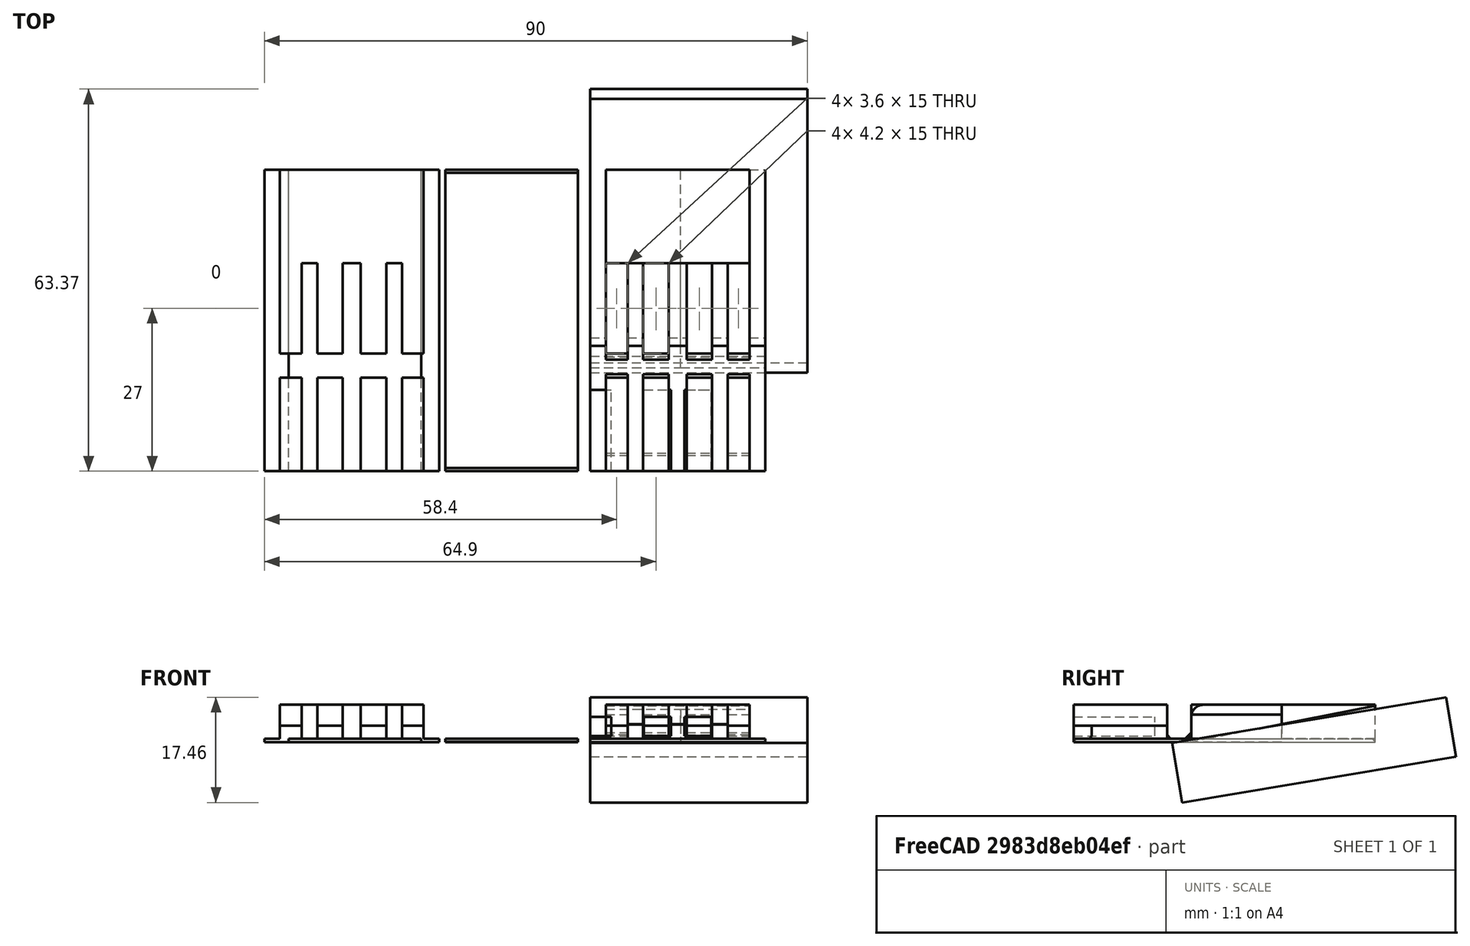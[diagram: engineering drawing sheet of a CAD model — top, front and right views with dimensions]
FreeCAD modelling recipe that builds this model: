
FCSTD DOCUMENT  (FreeCAD 0.19R24267 +99 (Git))
Label: TEST
License: All rights reserved
LicenseURL: http://en.wikipedia.org/wiki/All_rights_reserved
objects: Part::Box×15, Part::Cut×7, Part::Feature×5, Part::Chamfer×5, Mesh::Feature×4, PartDesign::FeatureBase×1, Sketcher::SketchObject×1, PartDesign::Pad×1, PartDesign::Body×1, Part::MultiFuse×1, Part::Fillet×1
note: 39 computed .brp shape members not serialized (recipe doc carries the construction recipe); baked Part::Feature solids carry a one-line shape summary decoded from their .brp

FEATURE [Part::Box] Box  label="Cube"
  AttacherType = Attacher::AttachEngine3D
  Height = 0.6
  Length = 29
  Width = 50
FEATURE [Part::Box] Box001  label="Cube001"
  AttacherType = Attacher::AttachEngine3D
  Height = 0.6
  Length = 22
  Placement = pos=(-50,0,0) rot=(0,0,1;0rad)
  Width = 50
FEATURE [Part::Box] Box002  label="Cube002"
  AttacherType = Attacher::AttachEngine3D
  Height = 3.2
  Length = 3.5
  Placement = pos=(0,0,1) rot=(0,0,1;0rad)
  Width = 13.5
FEATURE [Part::Box] Box003  label="Cube003"
  AttacherType = Attacher::AttachEngine3D
  Height = 3.2
  Length = 4.5
  Placement = pos=(8.9,0,1) rot=(0,0,1;0rad)
  Width = 13.5
FEATURE [Part::Box] Box004  label="Cube004"
  AttacherType = Attacher::AttachEngine3D
  Height = 3.2
  Length = 4.5
  Placement = pos=(15.6,0,1) rot=(0,0,1;0rad)
  Width = 13.5
FEATURE [PartDesign::FeatureBase] BaseFeature
  BaseFeature = -> Box
FEATURE [Sketcher::SketchObject] Sketch
  FullyConstrained = true
  MapMode = 5
  Support = -> [XY_Plane]
  sketch-geometry (37):
    g0: LineSegment StartX=14.5 StartY=55 StartZ=0 EndX=14.5 EndY=-13 EndZ=0
    g1: LineSegment StartX=-8 StartY=15.5 StartZ=0 EndX=37 EndY=15.5 EndZ=0
    g2: LineSegment StartX=-8 StartY=32 StartZ=0 EndX=37 EndY=32 EndZ=0
    g3: LineSegment StartX=13.3 StartY=18.5 StartZ=0 EndX=13.3 EndY=-2.5 EndZ=0
    g4: LineSegment StartX=15.7 StartY=18.5 StartZ=0 EndX=15.7 EndY=-2.5 EndZ=0
    g5: LineSegment StartX=8.8 StartY=15.5 StartZ=0 EndX=13 EndY=15.5 EndZ=0
    g6: LineSegment StartX=13 StartY=15.5 StartZ=0 EndX=13 EndY=0 EndZ=0
    g7: LineSegment StartX=13 StartY=0 StartZ=0 EndX=8.8 EndY=0 EndZ=0
    g8: LineSegment StartX=8.8 StartY=0 StartZ=0 EndX=8.8 EndY=15.5 EndZ=0
    g9: LineSegment StartX=2.6 StartY=15.5 StartZ=0 EndX=6.2 EndY=15.5 EndZ=0
    g10: LineSegment StartX=6.2 StartY=15.5 StartZ=0 EndX=6.2 EndY=0 EndZ=0
    g11: LineSegment StartX=6.2 StartY=4e-16 StartZ=0 EndX=2.6 EndY=4e-16 EndZ=0
    g12: LineSegment StartX=2.6 StartY=4e-16 StartZ=0 EndX=2.6 EndY=15.5 EndZ=0
    g13: LineSegment StartX=16 StartY=15.5 StartZ=0 EndX=20.2 EndY=15.5 EndZ=0
    g14: LineSegment StartX=20.2 StartY=15.5 StartZ=0 EndX=20.2 EndY=0 EndZ=0
    g15: LineSegment StartX=20.2 StartY=0 StartZ=0 EndX=16 EndY=0 EndZ=0
    g16: LineSegment StartX=16 StartY=0 StartZ=0 EndX=16 EndY=15.5 EndZ=0
    g17: LineSegment StartX=22.8 StartY=15.5 StartZ=0 EndX=26.4 EndY=15.5 EndZ=0
    g18: LineSegment StartX=26.4 StartY=15.5 StartZ=0 EndX=26.4 EndY=0 EndZ=0
    g19: LineSegment StartX=26.4 StartY=0 StartZ=0 EndX=22.8 EndY=0 EndZ=0
    g20: LineSegment StartX=22.8 StartY=0 StartZ=0 EndX=22.8 EndY=15.5 EndZ=0
    g21: LineSegment StartX=2.6 StartY=34.5 StartZ=0 EndX=6.2 EndY=34.5 EndZ=0
    g22: LineSegment StartX=6.2 StartY=34.5 StartZ=0 EndX=6.2 EndY=19.5 EndZ=0
    g23: LineSegment StartX=6.2 StartY=19.5 StartZ=0 EndX=2.6 EndY=19.5 EndZ=0
    g24: LineSegment StartX=2.6 StartY=19.5 StartZ=0 EndX=2.6 EndY=34.5 EndZ=0
    g25: LineSegment StartX=8.8 StartY=34.5 StartZ=0 EndX=13 EndY=34.5 EndZ=0
    g26: LineSegment StartX=13 StartY=34.5 StartZ=0 EndX=13 EndY=19.5 EndZ=0
    g27: LineSegment StartX=13 StartY=19.5 StartZ=0 EndX=8.8 EndY=19.5 EndZ=0
    g28: LineSegment StartX=8.8 StartY=19.5 StartZ=0 EndX=8.8 EndY=34.5 EndZ=0
    g29: LineSegment StartX=16 StartY=34.5 StartZ=0 EndX=20.2 EndY=34.5 EndZ=0
    g30: LineSegment StartX=20.2 StartY=34.5 StartZ=0 EndX=20.2 EndY=19.5 EndZ=0
    g31: LineSegment StartX=20.2 StartY=19.5 StartZ=0 EndX=16 EndY=19.5 EndZ=0
    g32: LineSegment StartX=16 StartY=19.5 StartZ=0 EndX=16 EndY=34.5 EndZ=0
    g33: LineSegment StartX=22.8 StartY=34.5 StartZ=0 EndX=26.4 EndY=34.5 EndZ=0
    g34: LineSegment StartX=26.4 StartY=34.5 StartZ=0 EndX=26.4 EndY=19.5 EndZ=0
    g35: LineSegment StartX=26.4 StartY=19.5 StartZ=0 EndX=22.8 EndY=19.5 EndZ=0
    g36: LineSegment StartX=22.8 StartY=19.5 StartZ=0 EndX=22.8 EndY=34.5 EndZ=0
  constraints (112):
    c: Vertical(g0)
    c: Horizontal(g2)
    c: DistanceX(g-1,g0) = 14.5
    c: Vertical(g3)
    c: Vertical(g4)
    c: DistanceY(g-1,g1) = 15.5
    c: DistanceY(g0,g0) = 68
    c: Symmetric(g3,g4,g0)
    c: DistanceX(g3,g0) = 1.2
    c: Equal(g4,g3)
    c: DistanceY(g4,g4) = 21
    c: Symmetric(g1,g1,g0)
    c: DistanceX(g1,g1) = 45
    c: Equal(g2,g1)
    c: Vertical(g2,g1)
    c: DistanceY(g-1,g0) = 55
    c: DistanceY(g4,g-1) = 2.5
    c: DistanceY(g-1,g2) = 32
    c: Coincident(g5,g6)
    c: Coincident(g6,g7)
    c: Coincident(g7,g8)
    c: Coincident(g8,g5)
    c: Horizontal(g5)
    c: Horizontal(g7)
    c: Vertical(g6)
    c: Vertical(g8)
    c: DistanceX(g5,g5) = 4.2
    c: DistanceY(g8,g8) = 15.5
    c: DistanceX(g6,g3) = 0.3
    c: DistanceY(g5,g1) = 0
    c: Coincident(g9,g10)
    c: Coincident(g10,g11)
    c: Coincident(g11,g12)
    c: Coincident(g12,g9)
    c: Horizontal(g9)
    c: Horizontal(g11)
    c: Vertical(g10)
    c: Vertical(g12)
    c: DistanceX(g9,g9) = 3.6
    c: DistanceY(g12,g12) = 15.5
    c: DistanceY(g6,g10) = 0
    c: DistanceX(g9,g5) = 2.6
    c: Coincident(g13,g14)
    c: Coincident(g14,g15)
    c: Coincident(g15,g16)
    c: Coincident(g16,g13)
    c: Horizontal(g13)
    c: Horizontal(g15)
    c: Vertical(g14)
    c: Vertical(g16)
    c: Coincident(g17,g18)
    c: Coincident(g18,g19)
    c: Coincident(g19,g20)
    c: Coincident(g20,g17)
    c: Horizontal(g17)
    c: Horizontal(g19)
    c: Vertical(g18)
    c: Vertical(g20)
    c: Equal(g5,g13)
    c: Equal(g6,g14)
    c: Symmetric(g13,g5,g0)
    c: Equal(g20,g10)
    c: Equal(g17,g11)
    c: Symmetric(g17,g9,g0)
    c: Coincident(g21,g22)
    c: Coincident(g22,g23)
    c: Coincident(g23,g24)
    c: Coincident(g24,g21)
    c: Horizontal(g21)
    c: Horizontal(g23)
    c: Vertical(g22)
    c: Vertical(g24)
    c: Coincident(g25,g26)
    c: Coincident(g26,g27)
    c: Coincident(g27,g28)
    c: Coincident(g28,g25)
    c: Horizontal(g25)
    c: Horizontal(g27)
    c: Vertical(g26)
    c: Vertical(g28)
    c: Coincident(g29,g30)
    c: Coincident(g30,g31)
    c: Coincident(g31,g32)
    c: Coincident(g32,g29)
    c: Horizontal(g29)
    c: Horizontal(g31)
    c: Vertical(g30)
    c: Vertical(g32)
    c: Coincident(g33,g34)
    c: Coincident(g34,g35)
    c: Coincident(g35,g36)
    c: Coincident(g36,g33)
    c: Horizontal(g33)
    c: Horizontal(g35)
    c: Vertical(g34)
    c: Vertical(g36)
    c: Equal(g27,g5)
    c: Equal(g5,g31)
    c: Equal(g35,g17)
    c: Equal(g17,g23)
    c: Horizontal(g35,g30)
    c: Horizontal(g30,g26)
    c: Horizontal(g26,g22)
    c: Equal(g24,g28)
    c: Equal(g28,g32)
    c: Equal(g32,g36)
    c: Vertical(g34,g17)
    c: Vertical(g30,g13)
    c: Vertical(g27,g5)
    c: Vertical(g23,g9)
    c: DistanceY(g17,g34) = 4
    c: DistanceY(g17,g33) = 19
FEATURE [PartDesign::Pad] Pad
  BaseFeature = -> BaseFeature
  Direction = (1,1,1)
  Length = 6.2
  Length2 = 100
  Profile = -> Sketch
  Type = 0
FEATURE [PartDesign::Body] Body
  BaseFeature = -> Box
  Group = -> [BaseFeature,Sketch,Pad]
  Origin = -> Origin
  Tip = -> Pad
FEATURE [Part::Feature] Body001
  shape: bbox 29 x 50 x 4.6 mm, 62 faces (baked)
FEATURE [Part::Box] Box005  label="Cube005"
  AttacherType = Attacher::AttachEngine3D
  Height = 10
  Length = 35
  Placement = pos=(0,0,2.75) rot=(0,0,1;0rad)
  Width = 18
FEATURE [Part::Cut] Cut
  Base = -> Body001
  Tool = -> Box005
FEATURE [Part::Box] Box006  label="Cube006"
  AttacherType = Attacher::AttachEngine3D
  Height = 6.2
  Length = 23.8
  Placement = pos=(2.6,34.5,0) rot=(0,0,1;0rad)
  Width = 15.5
FEATURE [Part::Feature] Body002
  shape: bbox 29 x 50 x 6.2 mm, 62 faces (baked)
FEATURE [Part::Box] Box009  label="Cube009"
  AttacherType = Attacher::AttachEngine3D
  Height = 10
  Length = 35
  Placement = pos=(0,0,2.75) rot=(0,0,1;0rad)
  Width = 18
FEATURE [Part::Cut] Cut001
  Base = -> Body002
  Tool = -> Box009
FEATURE [Part::MultiFuse] Fusion  label="pieza2"
  Placement = pos=(-54,0,0) rot=(0,0,1;0rad)
  Shapes = -> [Box006,Cut001]
FEATURE [Part::Box] Box010  label="Cube010"
  AttacherType = Attacher::AttachEngine3D
  Height = 0.6
  Length = 22
  Placement = pos=(-24,0,0) rot=(0,0,1;0rad)
  Width = 50
FEATURE [Part::Chamfer] Chamfer
  Base = -> Box010
  Edges = 2 edges r=0.5: [Edge10,Edge12]
FEATURE [Mesh::Feature] Mesh  label="pieza_2"
FEATURE [Mesh::Feature] Mesh001  label="pieza_1"
FEATURE [Part::Feature] Fusion001  label="pieza003"
  shape: bbox 29 x 50 x 6.2 mm, 68 faces (baked)
FEATURE [Part::Box] Box011  label="Cube011"
  AttacherType = Attacher::AttachEngine3D
  Height = 10
  Length = 7
  Placement = pos=(0,18,-10) rot=(1,0,0;0.165806rad)
  Width = 46
FEATURE [Part::Box] Box012  label="Cube012"
  AttacherType = Attacher::AttachEngine3D
  Height = 10
  Length = 8
  Placement = pos=(7,18,-10) rot=(1,0,0;0.165806rad)
  Width = 46
FEATURE [Part::Box] Box013  label="Cube013"
  AttacherType = Attacher::AttachEngine3D
  Height = 10
  Length = 36
  Placement = pos=(0,18,-10) rot=(1,0,0;0.165806rad)
  Width = 46
FEATURE [Part::Box] Box014  label="Cube014"
  AttacherType = Attacher::AttachEngine3D
  Height = 10
  Length = 36
  Placement = pos=(0,18,-10) rot=(1,0,0;0.165806rad)
  Width = 46
FEATURE [Part::Cut] Cut002
  Base = -> Fusion001
  Tool = -> Box011
FEATURE [Part::Cut] Cut003
  Base = -> Cut002
  Tool = -> Box012
FEATURE [Part::Cut] Cut004  label="pieza_3"
  Base = -> Cut003
  Tool = -> Box013
FEATURE [Part::Chamfer] Chamfer001
  Base = -> Cut004
  Edges = 4 edges r=1: [Edge74,Edge77,Edge80,Edge83]
FEATURE [Mesh::Feature] Mesh002  label="pieza_03"
FEATURE [Part::Feature] Cut003001
  shape: bbox 29 x 50 x 6.2 mm, 68 faces (baked)
FEATURE [Part::Box] Box015  label="Cube015"
  AttacherType = Attacher::AttachEngine3D
  Height = 10
  Length = 36
  Placement = pos=(0,20,-10) rot=(1,0,0;0.191986rad)
  Width = 46
FEATURE [Part::Box] Box016  label="Cube016"
  AttacherType = Attacher::AttachEngine3D
  Height = 10
  Length = 34
  Placement = pos=(0,0,0.6) rot=(0,0,1;0rad)
  Width = 3
FEATURE [Part::Feature] Fusion002  label="pieza004"
  shape: bbox 29 x 50 x 6.2 mm, 68 faces (baked)
FEATURE [Part::Cut] Cut003002
  Base = -> Fusion002
  Tool = -> Box016
FEATURE [Part::Cut] Cut003003
  Base = -> Cut003002
  Tool = -> Box015
FEATURE [Part::Chamfer] Chamfer002
  Base = -> Cut003003
  Edges = 4 edges r=0.6: [Edge76,Edge80,Edge84,Edge88]
FEATURE [Part::Chamfer] Chamfer003
  Base = -> Chamfer002
  Edges = 4 edges r=0.6: [Edge7,Edge11,Edge15,Edge19]
FEATURE [Part::Fillet] Fillet
  Base = -> Chamfer003
  Edges = 4 edges r=2: [Edge161,Edge188,Edge195,Edge203]
FEATURE [Part::Chamfer] Chamfer004  label="pieza_4"
  Base = -> Fillet
  Edges = 4 edges r=0.4: [Edge207,Edge211,Edge217,Edge223]
FEATURE [Mesh::Feature] Mesh003  label="pieza_4 (Meshed)"
